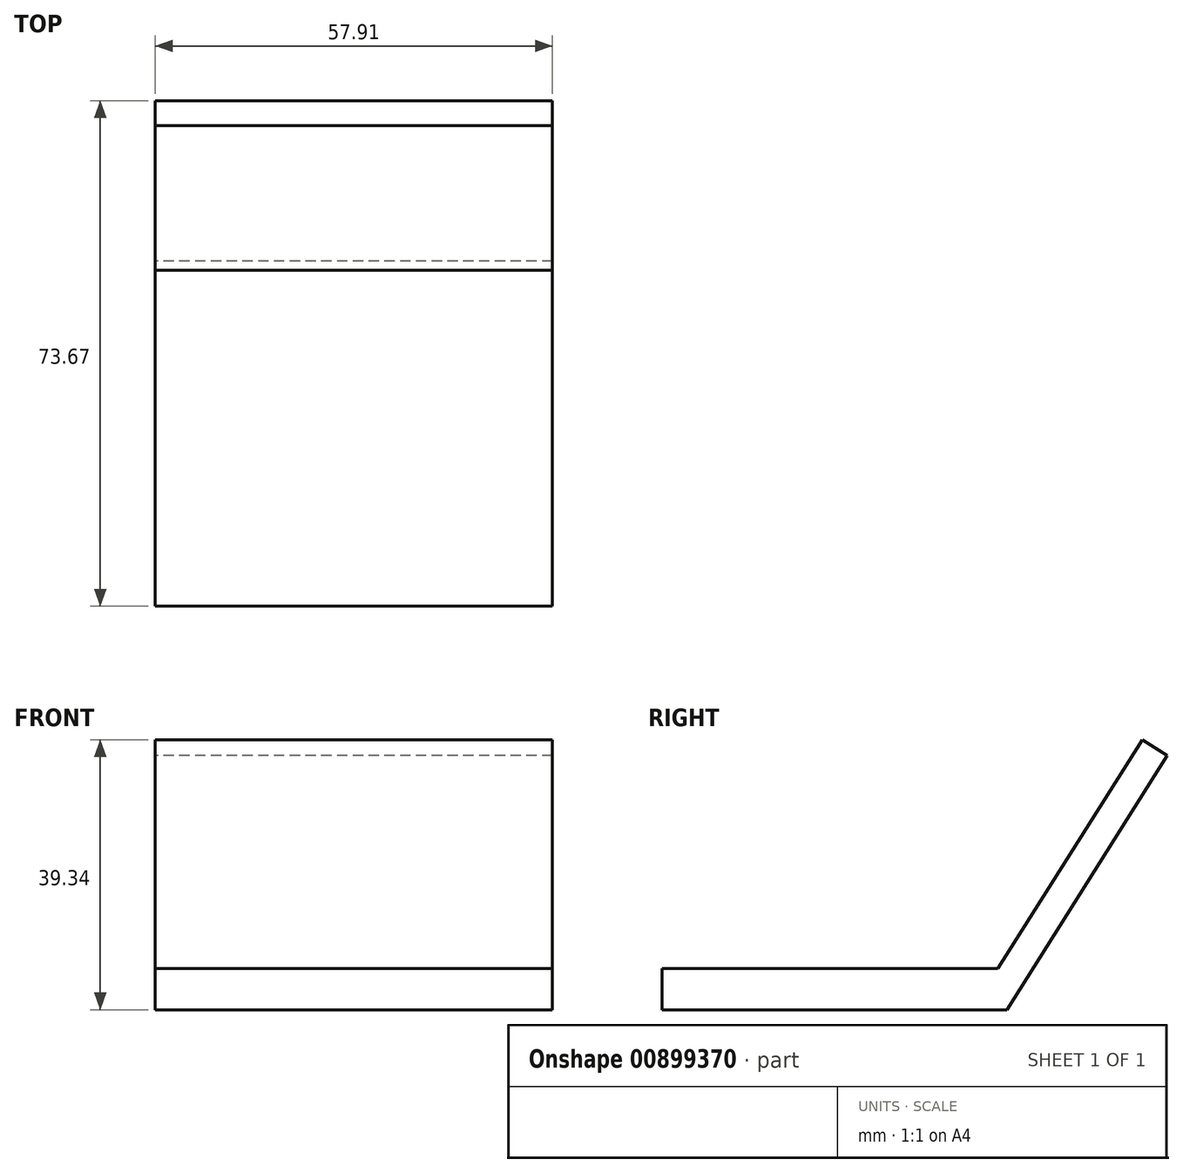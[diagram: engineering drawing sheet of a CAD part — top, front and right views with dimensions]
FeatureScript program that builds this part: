
annotation { "Feature Type Name" : "Feature", "Feature Type Description" : "" }
export const myFeature = defineFeature(function(context is Context, id is Id, definition is map)
    precondition{}
    {
        {
            var Q0;
            Q0=qCreatedBy(makeId("Right.planeOp"),FACE);
            var sketch = newSketch(context, id + "F0", { "sketchPlane" : qUnion([Q0])});
            skLineSegment(sketch, "E0.bottom", {"start": v(-56.08, 0) * mm, "end": v(-7.1, 0) * mm});
            skLineSegment(sketch, "E0.top", {"start": v(-56.08, 6.03) * mm, "end": v(-7.1, 6.03) * mm});
            skLineSegment(sketch, "E0.left", {"start": v(-56.08, 0) * mm, "end": v(-56.08, 6.03) * mm});
            skLineSegment(sketch, "E1", {"start": v(-7.1, 6.03) * mm, "end": v(13.94, 39.34) * mm});
            skLineSegment(sketch, "E2", {"start": v(13.94, 39.34) * mm, "end": v(17.6, 37.03) * mm});
            skLineSegment(sketch, "E3", {"start": v(17.6, 37.03) * mm, "end": v(-5.8, 0) * mm});
            skLineSegment(sketch, "E4", {"start": v(-5.8, 0) * mm, "end": v(-7.1, 0) * mm});
            skSolve(sketch);
        }
        {
            var Q0;
            Q0 = qSketchRegion(id + "F0", true);
            extrude(context, id + "F1", {"entities" : qUnion([Q0]), "depth" : 57.9 * mm, "offsetDistance" : 25.4 * mm});
        }
    });
